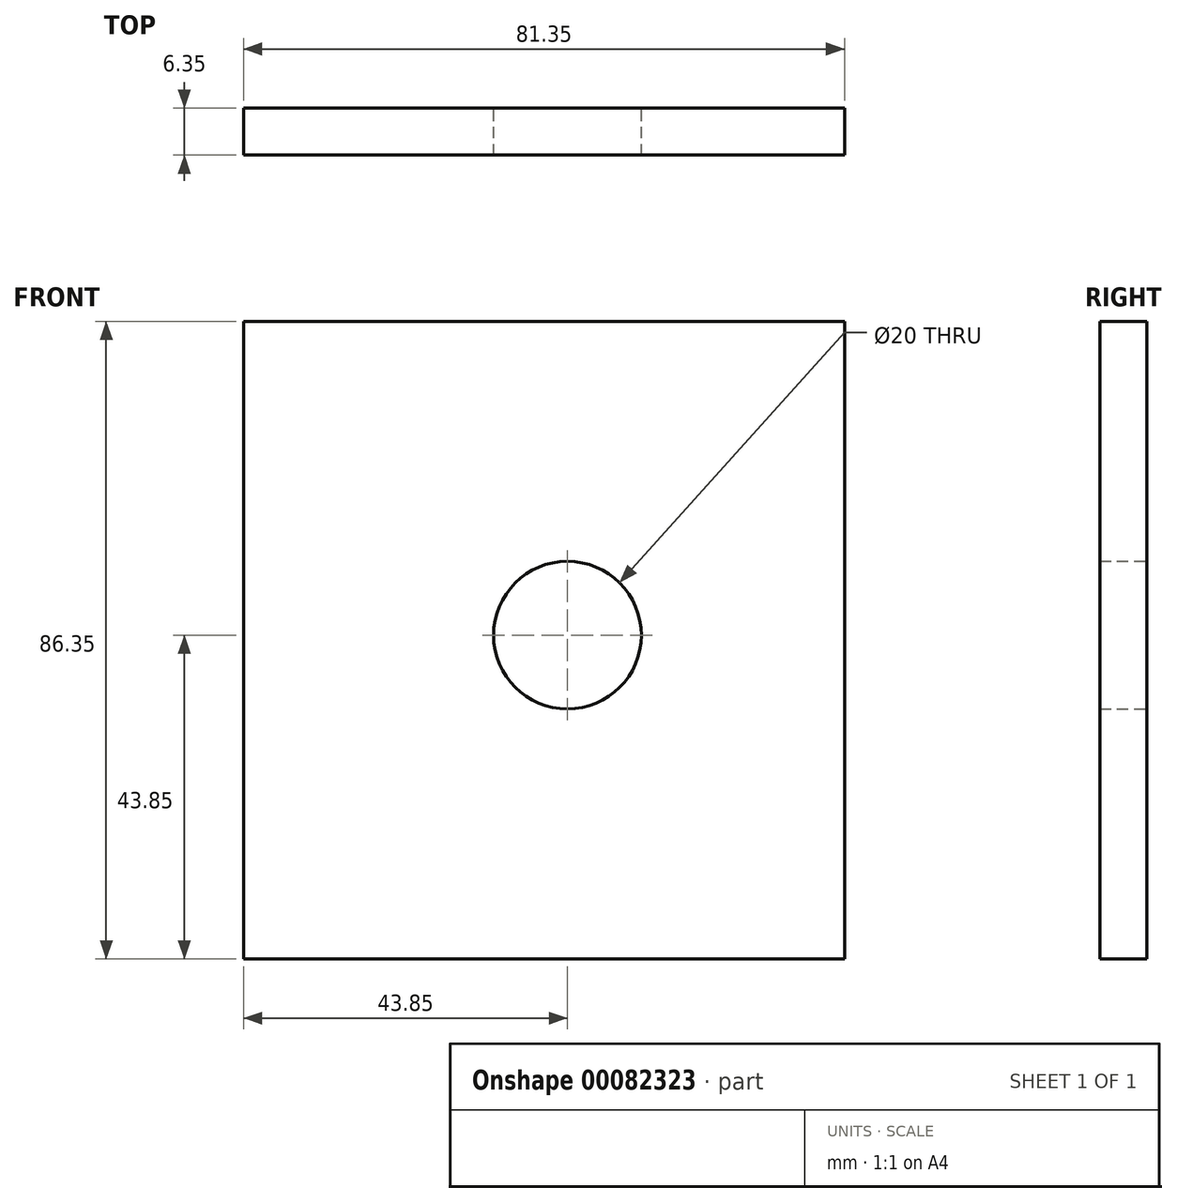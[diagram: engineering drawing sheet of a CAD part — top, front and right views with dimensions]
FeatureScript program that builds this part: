
annotation { "Feature Type Name" : "Feature", "Feature Type Description" : "" }
export const myFeature = defineFeature(function(context is Context, id is Id, definition is map)
    precondition{}
    {
        {
            var Q0;
            Q0=qCreatedBy(makeId("Front.planeOp"),FACE);
            var sketch = newSketch(context, id + "F0", { "sketchPlane" : qUnion([Q0])});
            skLineSegment(sketch, "E0.bottom", {"start": v(37.5, -37.5) * mm, "end": v(-37.5, -37.5) * mm});
            skLineSegment(sketch, "E0.top", {"start": v(37.5, 37.5) * mm, "end": v(-37.5, 37.5) * mm});
            skLineSegment(sketch, "E0.left", {"start": v(37.5, -37.5) * mm, "end": v(37.5, 37.5) * mm});
            skLineSegment(sketch, "E0.right", {"start": v(-37.5, -37.5) * mm, "end": v(-37.5, 37.5) * mm});
            skPoint(sketch, "E0.middle", {"position": v(0, 0) * mm});
            skCircle(sketch, "E1", {"center": v(0, 0) * mm, "radius": 10 * mm});
            skCircle(sketch, "E2", {"center": v(0, -27.5) * mm, "radius": 2.39 * mm});
            skLineSegment(sketch, "E3.bottom", {"start": v(37.5, 37.5) * mm, "end": v(-43.85, 37.5) * mm});
            skLineSegment(sketch, "E3.top", {"start": v(37.5, -43.85) * mm, "end": v(-43.85, -43.85) * mm});
            skLineSegment(sketch, "E3.left", {"start": v(37.5, 37.5) * mm, "end": v(37.5, -43.85) * mm});
            skLineSegment(sketch, "E3.right", {"start": v(-43.85, 37.5) * mm, "end": v(-43.85, -43.85) * mm});
            skLineSegment(sketch, "E4", {"start": v(-37.5, -37.5) * mm, "end": v(-43.85, -37.5) * mm});
            skLineSegment(sketch, "E5", {"start": v(-37.5, -37.5) * mm, "end": v(-37.5, -43.85) * mm});
            skLineSegment(sketch, "E6", {"start": v(0, 0) * mm, "end": v(0, -37.5) * mm, "construction": true});
            skLineSegment(sketch, "E7", {"start": v(-43.85, 37.5) * mm, "end": v(-43.85, 42.5) * mm});
            skLineSegment(sketch, "E8", {"start": v(37.5, 37.5) * mm, "end": v(37.5, 42.5) * mm});
            skLineSegment(sketch, "E9", {"start": v(-43.85, 42.5) * mm, "end": v(37.5, 42.5) * mm});
            skSolve(sketch);
        }
        {
            var Q0;
            Q0=makeQuery(id+"F0.imprint","IMPRINT",FACE,{"disambiguationData":[TD([[makeQuery(id+"F0.imprint","IMPRINT",EDGE,{"derivedFrom":sQuery(id+"F0.wireOp",EDGE,"E0.bottom")}),-1.0]])]});
            var Q1;
            {var subQ0=sQuery(id+"F0.wireOp",EDGE,"E0.right");Q1=makeQuery(id+"F0.imprint","IMPRINT",FACE,{"disambiguationData":[TD([[makeQuery(id+"F0.imprint","IMPRINT",EDGE,{"derivedFrom":subQ0}),1.0]])]});}
            var Q2;
            {var subQ4=sQuery(id+"F0.wireOp",EDGE,"E4");Q2=makeQuery(id+"F0.imprint","IMPRINT",FACE,{"disambiguationData":[TD([[makeQuery(id+"F0.imprint","IMPRINT",EDGE,{"derivedFrom":subQ4}),1.0]])]});}
            var Q3;
            {var subQ0=sQuery(id+"F0.wireOp",EDGE,"E0.bottom");Q3=makeQuery(id+"F0.imprint","IMPRINT",FACE,{"disambiguationData":[TD([[makeQuery(id+"F0.imprint","IMPRINT",EDGE,{"derivedFrom":subQ0}),1.0]])]});}
            var Q4;
            {var subQ1=sQuery(id+"F0.wireOp",EDGE,"E7");Q4=makeQuery(id+"F0.imprint","IMPRINT",FACE,{"disambiguationData":[TD([[makeQuery(id+"F0.imprint","IMPRINT",EDGE,{"derivedFrom":subQ1}),-1.0]])]});}
            var Q5;
            Q5=makeQuery(id+"F0.imprint","IMPRINT",FACE,{"disambiguationData":[TD([[makeQuery(id+"F0.imprint","IMPRINT",EDGE,{"derivedFrom":sQuery(id+"F0.wireOp",EDGE,"E2")}),1.0]])]});
            extrude(context, id + "F1", {"entities" : qUnion([Q0, Q1, Q2, Q3, Q4, Q5]), "depth" : 6.35 * mm});
        }
    });
